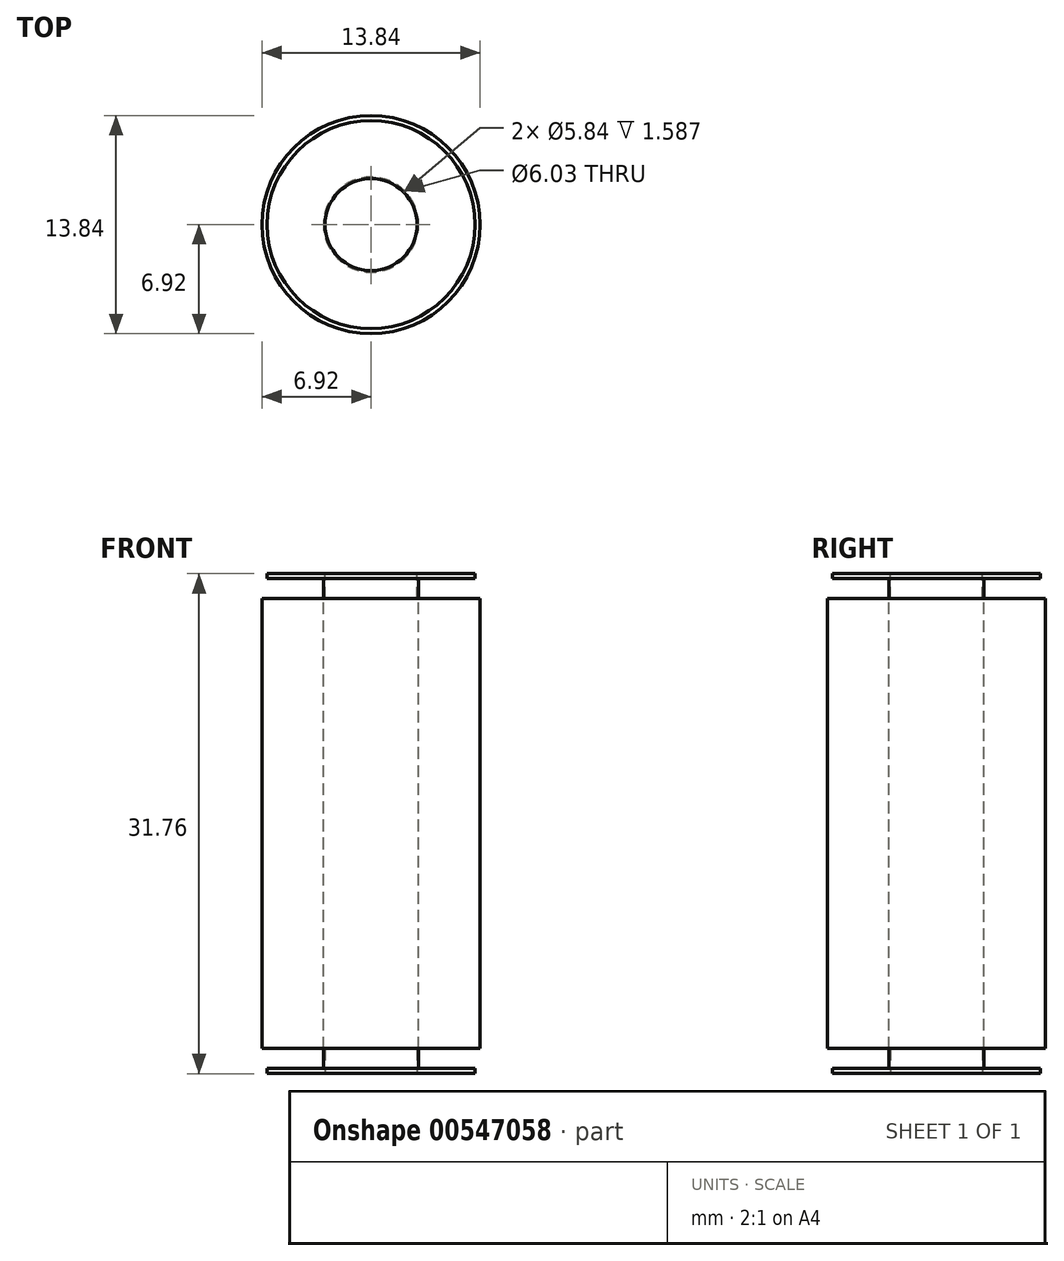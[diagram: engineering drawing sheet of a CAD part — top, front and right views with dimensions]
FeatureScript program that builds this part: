
annotation { "Feature Type Name" : "Feature", "Feature Type Description" : "" }
export const myFeature = defineFeature(function(context is Context, id is Id, definition is map)
    precondition{}
    {
        {
            var Q0;
            Q0=qCreatedBy(makeId("Top.planeOp"),FACE);
            var sketch = newSketch(context, id + "F0", { "sketchPlane" : qUnion([Q0])});
            skCircle(sketch, "E0", {"center": v(0, 0) * mm, "radius": 6.92 * mm});
            skSolve(sketch);
        }
        {
            var Q0;
            Q0 = qSketchRegion(id + "F0", true);
            extrude(context, id + "F1", {"entities" : qUnion([Q0]), "endBound" : BoundingType.SYMMETRIC, "depth" : 28.57 * mm, "offsetDistance" : 25.4 * mm});
        }
        {
            var Q0;
            Q0=makeQuery(id+"F1.opExtrude","CAP_FACE",FACE,{"disambiguationData":[OSD([sQuery(id+"F0.wireOp",EDGE,"E0")])],"isStart":false});
            var sketch = newSketch(context, id + "F2", { "sketchPlane" : qUnion([Q0])});
            skCircle(sketch, "E1", {"center": v(0, 0) * mm, "radius": 3.02 * mm});
            skSolve(sketch);
        }
        {
            var Q0;
            Q0 = qSketchRegion(id + "F2", true);
            extrude(context, id + "F3", {"entities" : qUnion([Q0]), "operationType" : NewBodyOperationType.REMOVE, "endBound" : BoundingType.THROUGH_ALL, "oppositeDirection" : true, "depth" : 25.4 * mm, "offsetDistance" : 25.4 * mm});
        }
        {
            var Q0;
            Q0=makeQuery(id+"F1.opExtrude","CAP_FACE",FACE,{"disambiguationData":[OSD([sQuery(id+"F0.wireOp",EDGE,"E0")])],"isStart":false});
            var sketch = newSketch(context, id + "F4", { "sketchPlane" : qUnion([Q0])});
            skCircle(sketch, "E2", {"center": v(0, 0) * mm, "radius": 3.02 * mm});
            skSolve(sketch);
        }
        {
            var Q0;
            Q0 = qSketchRegion(id + "F4", true);
            extrude(context, id + "F5", {"entities" : qUnion([Q0]), "depth" : 1.59 * mm, "offsetDistance" : 25.4 * mm});
        }
        {
            var Q0;
            Q0=makeQuery(id+"F5.opExtrude","CAP_FACE",FACE,{"disambiguationData":[OSD([sQuery(id+"F4.wireOp",EDGE,"E2")])],"isStart":false});
            var Q1;
            Q1=makeQuery(id+"F5.opExtrude","SWEPT_BODY",BODY,{"disambiguationData":[OSD([sQuery(id+"F4.wireOp",EDGE,"E2")])]});
            shell(context, id + "F6", {"entities" : qUnion([Q0]), "parts" : qUnion([Q1]), "thickness" : 0.32 * mm});
        }
        {
            var Q0;
            Q0=makeQuery(id+"F5.opExtrude","CAP_FACE",FACE,{"disambiguationData":[OSD([sQuery(id+"F4.wireOp",EDGE,"E2")])],"isStart":false});
            var sketch = newSketch(context, id + "F7", { "sketchPlane" : qUnion([Q0])});
            skCircle(sketch, "E3", {"center": v(0, 0) * mm, "radius": 6.6 * mm});
            skSolve(sketch);
        }
        {
            var Q0;
            Q0 = qSketchRegion(id + "F7", true);
            var Q1;
            Q1=makeQuery(id+"F7.imprint","IMPRINT",FACE,{"disambiguationData":[TD([[makeQuery(id+"F7.imprint","IMPRINT",EDGE,{"derivedFrom":sQuery(id+"F7.wireOp",EDGE,"E3")}),1.0]])]});
            extrude(context, id + "F8", {"entities" : qUnion([Q0, Q1]), "operationType" : NewBodyOperationType.ADD, "oppositeDirection" : true, "depth" : 0.32 * mm, "offsetDistance" : 25.4 * mm});
        }
        {
            var Q0;
            Q0=makeQuery(id+"F8.boolean.opBoolean","MERGE",FACE,{"derivedFrom":[makeQuery(id+"F5.opExtrude","CAP_FACE",FACE,{"disambiguationData":[OSD([sQuery(id+"F4.wireOp",EDGE,"E2")])],"isStart":false}),makeQuery(id+"F8.opExtrude","CAP_FACE",FACE,{"disambiguationData":[OSD([sQuery(id+"F7.wireOp",EDGE,"E3")])],"isStart":true})]});
            var sketch = newSketch(context, id + "F9", { "sketchPlane" : qUnion([Q0])});
            skCircle(sketch, "E4", {"center": v(0, 0) * mm, "radius": 2.92 * mm});
            skSolve(sketch);
        }
        {
            var Q0;
            Q0 = qSketchRegion(id + "F9", true);
            extrude(context, id + "F10", {"entities" : qUnion([Q0]), "operationType" : NewBodyOperationType.REMOVE, "oppositeDirection" : true, "depth" : 25.4 * mm, "offsetDistance" : 25.4 * mm});
        }
        {
            var Q0;
            Q0=makeQuery(id+"F5.opExtrude","SWEPT_BODY",BODY,{"disambiguationData":[OSD([sQuery(id+"F4.wireOp",EDGE,"E2")])]});
            var Q1;
            Q1=qCreatedBy(makeId("Top.planeOp"),FACE);
            mirror(context, id + "F11", {"entities" : qUnion([Q0]), "mirrorPlane" : qUnion([Q1])});
        }
    });
